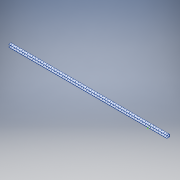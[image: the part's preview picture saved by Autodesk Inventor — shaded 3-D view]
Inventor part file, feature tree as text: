
AUTODESK INVENTOR PART (.ipt)
format: ipt  version: 2017 (Build 210142000, 142)  size: 301,568 bytes
history: native  units: in
note: dims shown in document units (in); Inventor stores cm internally (conversion verified against a paired STEP export)
features: sketch x1, other x1
ambient origin geometry x8: Origin, YZ Plane, XZ Plane, XY Plane, X Axis, Y Axis, Z Axis, Center Point
bodies: Solid1 (feature_tree)
feature tree (2):
  sketch  "Sketch1"
  other  "Break-Corner1"
